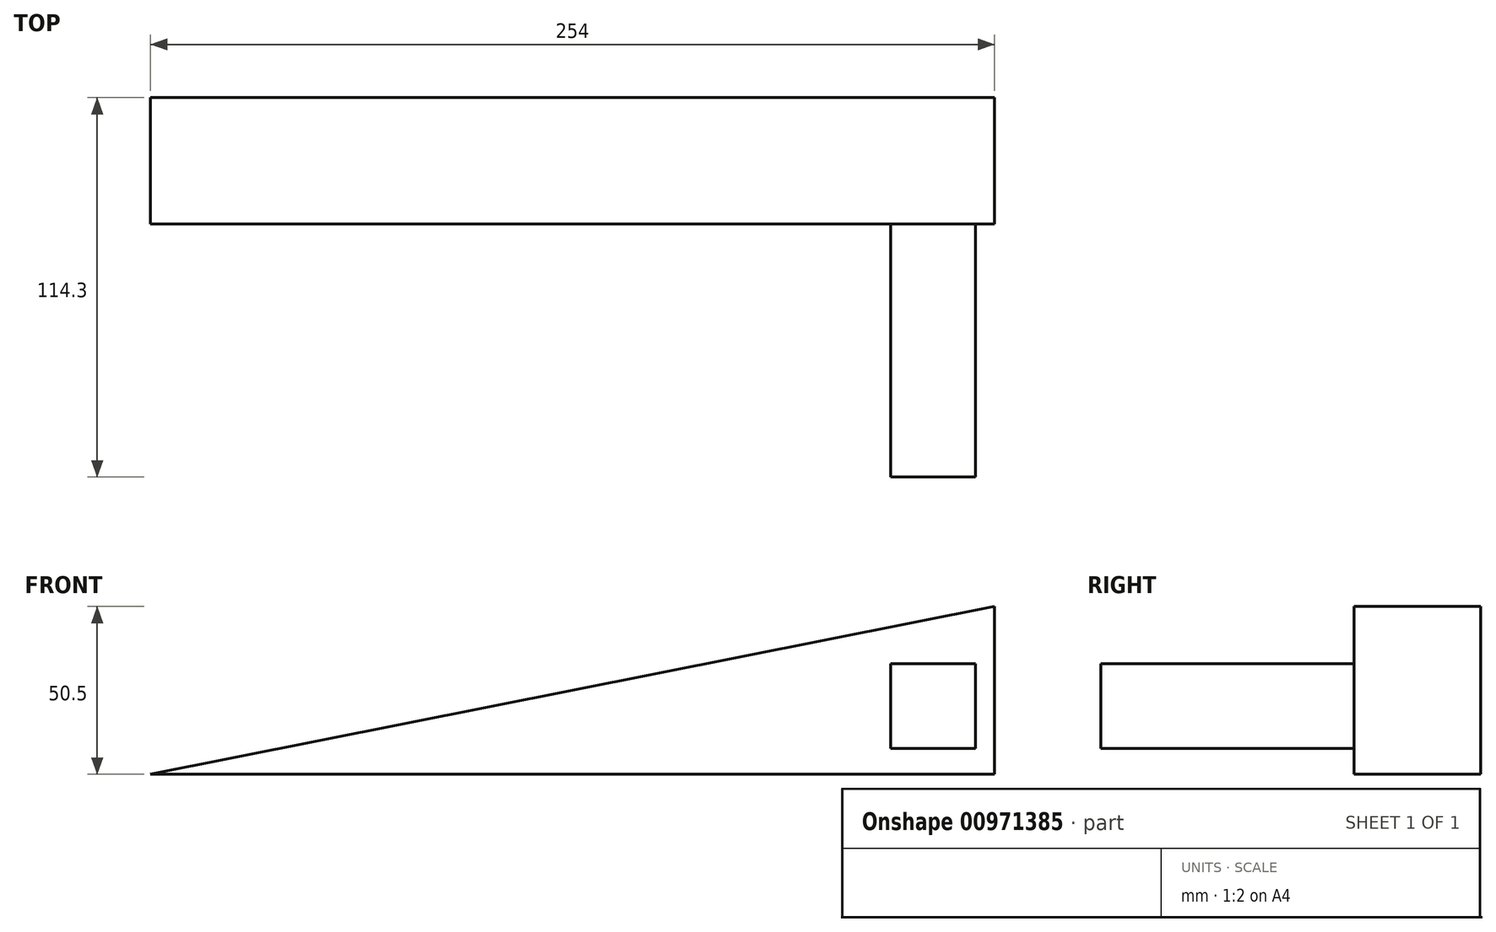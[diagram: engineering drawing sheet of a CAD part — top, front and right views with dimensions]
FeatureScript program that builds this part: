
annotation { "Feature Type Name" : "Feature", "Feature Type Description" : "" }
export const myFeature = defineFeature(function(context is Context, id is Id, definition is map)
    precondition{}
    {
        {
            var Q0;
            Q0=qCreatedBy(makeId("Front.planeOp"),FACE);
            var sketch = newSketch(context, id + "F0", { "sketchPlane" : qUnion([Q0])});
            skLineSegment(sketch, "E0", {"start": v(-149.12, 50.8) * mm, "end": v(104.88, 50.8) * mm});
            skLineSegment(sketch, "E1", {"start": v(104.88, 50.8) * mm, "end": v(104.88, 0) * mm});
            skLineSegment(sketch, "E2", {"start": v(104.88, 0) * mm, "end": v(-149.12, 0) * mm});
            skLineSegment(sketch, "E3", {"start": v(-149.12, 0) * mm, "end": v(-149.12, 50.8) * mm});
            skSolve(sketch);
        }
        {
            var Q0;
            Q0=makeQuery(id+"F0.imprint","IMPRINT",FACE,{"disambiguationData":[TD([[makeQuery(id+"F0.imprint","IMPRINT",EDGE,{"derivedFrom":sQuery(id+"F0.wireOp",EDGE,"E0")}),-1.0]])]});
            extrude(context, id + "F1", {"entities" : qUnion([Q0]), "depth" : 38.1 * mm, "offsetDistance" : 25.4 * mm});
        }
        {
            var Q0;
            {var subQ0=sQuery(id+"F0.wireOp",EDGE,"E3");var subQ1=sQuery(id+"F0.wireOp",EDGE,"E0");Q0=makeQuery(id+"Fwq3wJgdgd3FOB3_1.boolean.opBoolean","MERGE",EDGE,{"derivedFrom":[makeQuery(id+"F1.opExtrude","SWEPT_EDGE",EDGE,{"disambiguationData":[OSD([subQ1,subQ0])]}),makeQuery(id+"Fwq3wJgdgd3FOB3_1.opExtrude","SWEPT_EDGE",EDGE,{"disambiguationData":[OSD([subQ1,subQ0])]})]});}
            chamfer(context, id + "F2", {"entities" : qUnion([Q0]), "chamferType" : ChamferType.OFFSET_ANGLE, "width" : 50.8 * mm, "oppositeDirection" : false, "angle" : 78.75 * degree, "tangentPropagation" : true});
        }
        {
            var Q0;
            Q0=makeQuery(id+"F1.opExtrude","CAP_FACE",FACE,{"disambiguationData":[OSD([sQuery(id+"F0.wireOp",EDGE,"E0"),sQuery(id+"F0.wireOp",EDGE,"E1"),sQuery(id+"F0.wireOp",EDGE,"E2"),sQuery(id+"F0.wireOp",EDGE,"E3")])],"isStart":false});
            var sketch = newSketch(context, id + "F3", { "sketchPlane" : qUnion([Q0])});
            skLineSegment(sketch, "E4.bottom", {"start": v(99.08, 7.71) * mm, "end": v(73.54, 7.71) * mm});
            skLineSegment(sketch, "E4.top", {"start": v(99.08, 33.25) * mm, "end": v(73.54, 33.25) * mm});
            skLineSegment(sketch, "E4.left", {"start": v(99.08, 7.71) * mm, "end": v(99.08, 33.25) * mm});
            skLineSegment(sketch, "E4.right", {"start": v(73.54, 7.71) * mm, "end": v(73.54, 33.25) * mm});
            skSolve(sketch);
        }
        {
            var Q0;
            Q0 = qSketchRegion(id + "F3", true);
            extrude(context, id + "F4", {"entities" : qUnion([Q0]), "operationType" : NewBodyOperationType.ADD, "depth" : 76.2 * mm, "offsetDistance" : 25.4 * mm});
        }
    });
